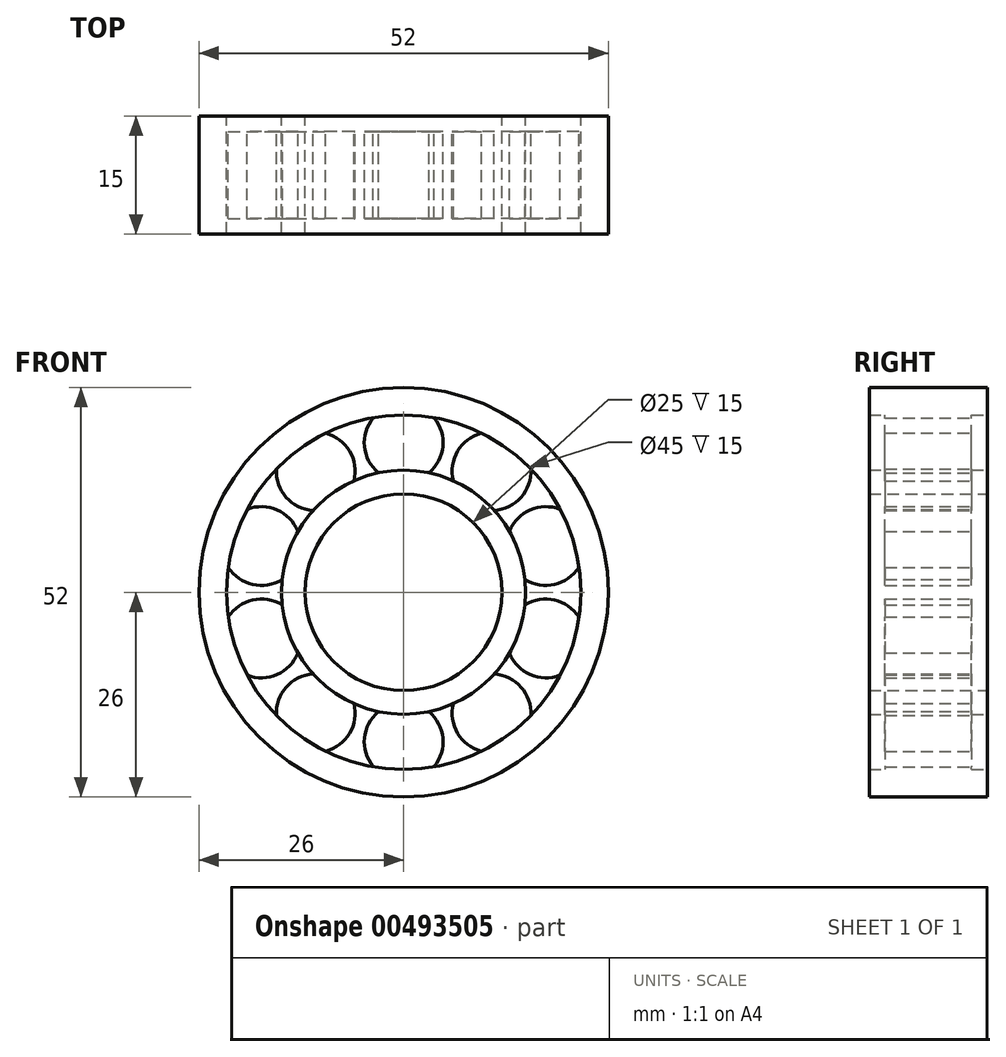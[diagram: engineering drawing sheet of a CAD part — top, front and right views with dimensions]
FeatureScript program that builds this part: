
annotation { "Feature Type Name" : "Feature", "Feature Type Description" : "" }
export const myFeature = defineFeature(function(context is Context, id is Id, definition is map)
    precondition{}
    {
        {
            var Q0;
            Q0=qCreatedBy(makeId("Front.planeOp"),FACE);
            var sketch = newSketch(context, id + "F0", { "sketchPlane" : qUnion([Q0])});
            skCircle(sketch, "E0", {"center": v(0, 0) * mm, "radius": 12.5 * mm});
            skCircle(sketch, "E1", {"center": v(0, 0) * mm, "radius": 15.5 * mm});
            skCircle(sketch, "E2", {"center": v(0, 0) * mm, "radius": 22.5 * mm});
            skCircle(sketch, "E3", {"center": v(0, 0) * mm, "radius": 26 * mm});
            skSolve(sketch);
        }
        {
            var Q0;
            Q0=makeQuery(id+"F0.imprint","IMPRINT",FACE,{"disambiguationData":[TD([[makeQuery(id+"F0.imprint","IMPRINT",EDGE,{"derivedFrom":sQuery(id+"F0.wireOp",EDGE,"E2")}),-1.0]])]});
            var Q1;
            Q1=makeQuery(id+"F0.imprint","IMPRINT",FACE,{"disambiguationData":[TD([[makeQuery(id+"F0.imprint","IMPRINT",EDGE,{"derivedFrom":sQuery(id+"F0.wireOp",EDGE,"E0")}),-1.0]])]});
            extrude(context, id + "F1", {"entities" : qUnion([Q0, Q1]), "endBound" : BoundingType.SYMMETRIC, "depth" : 15 * mm, "offsetDistance" : 25 * mm});
        }
        {
            var Q0;
            Q0=qCreatedBy(makeId("Front.planeOp"),FACE);
            var sketch = newSketch(context, id + "F2", { "sketchPlane" : qUnion([Q0])});
            skCircle(sketch, "E4", {"center": v(0, 19) * mm, "radius": 5 * mm});
            skSolve(sketch);
        }
        {
            var Q0;
            Q0=makeQuery(id+"F2.imprint","IMPRINT",FACE,{"disambiguationData":[TD([[makeQuery(id+"F2.imprint","IMPRINT",EDGE,{"derivedFrom":sQuery(id+"F2.wireOp",EDGE,"E4")}),1.0]])]});
            extrude(context, id + "F3", {"entities" : qUnion([Q0]), "endBound" : BoundingType.SYMMETRIC, "depth" : 11 * mm, "offsetDistance" : 25 * mm});
        }
        {
            var Q0;
            Q0=makeQuery(id+"F3.opExtrude","SWEPT_BODY",BODY,{"disambiguationData":[OSD([sQuery(id+"F2.wireOp",EDGE,"E4")])]});
            var Q1;
            Q1=makeQuery(id+"F1.opExtrude","CAP_EDGE",EDGE,{"disambiguationData":[OSD([sQuery(id+"F0.wireOp",EDGE,"E0")])],"isStart":false});
            circularPattern(context, id + "F4", {"operationType" : NewBodyOperationType.ADD, "entities" : qUnion([Q0]), "axis" : qUnion([Q1]), "angle" : 360 * degree, "instanceCount" : 10, "equalSpace" : true});
        }
    });
